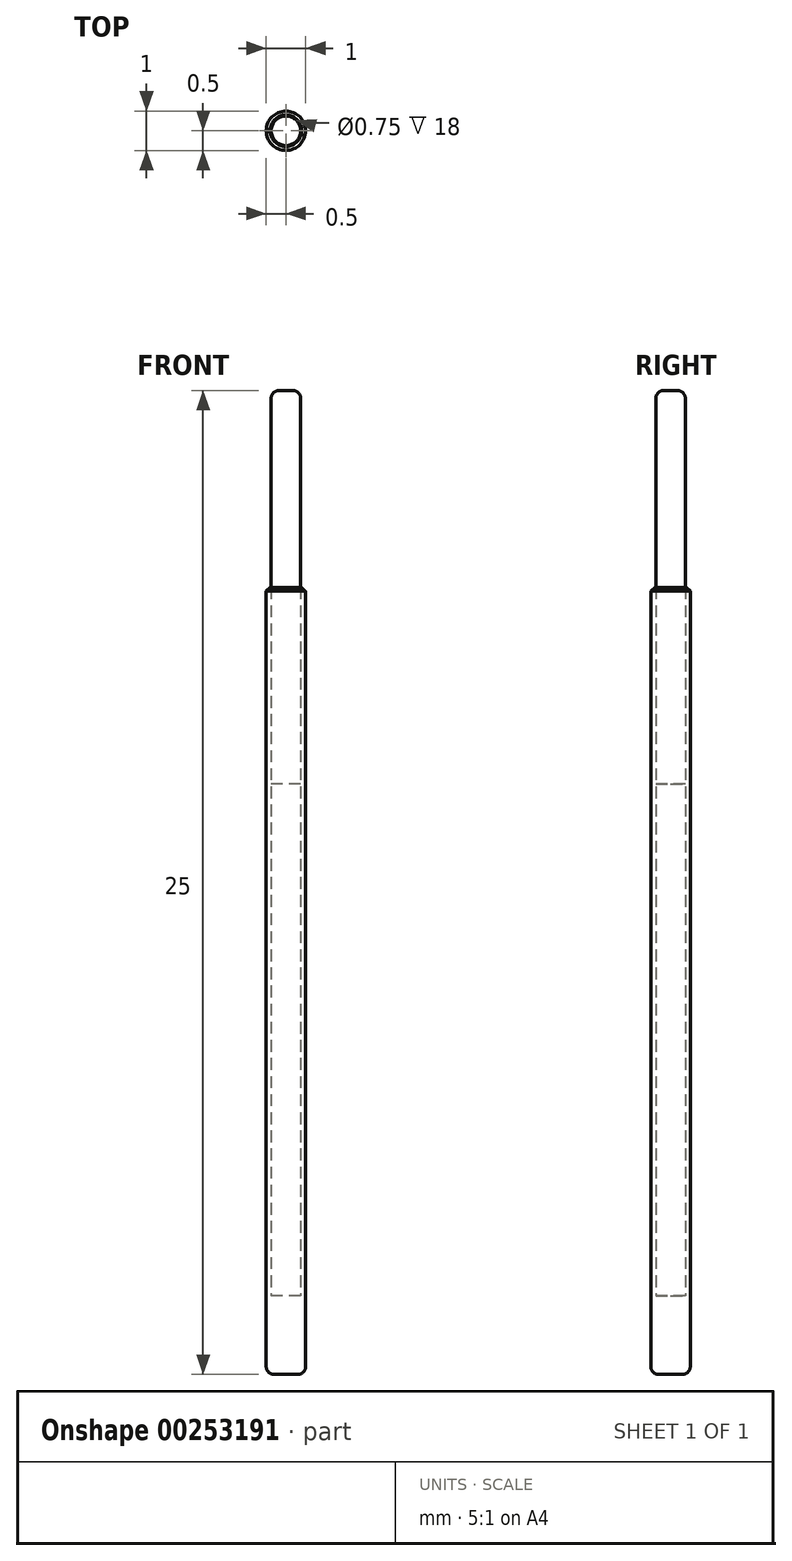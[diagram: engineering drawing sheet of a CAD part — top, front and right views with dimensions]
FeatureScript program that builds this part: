
annotation { "Feature Type Name" : "Feature", "Feature Type Description" : "" }
export const myFeature = defineFeature(function(context is Context, id is Id, definition is map)
    precondition{}
    {
        {
            var Q0;
            Q0=qCreatedBy(makeId("Top.planeOp"),FACE);
            var sketch = newSketch(context, id + "F0", { "sketchPlane" : qUnion([Q0])});
            skCircle(sketch, "E0", {"center": v(0, 0) * mm, "radius": 0.5 * mm});
            skCircle(sketch, "E1", {"center": v(0, 0) * mm, "radius": 0.38 * mm});
            skSolve(sketch);
        }
        {
            var Q0;
            Q0=makeQuery(id+"F0.imprint","IMPRINT",FACE,{"disambiguationData":[TD([[makeQuery(id+"F0.imprint","IMPRINT",EDGE,{"derivedFrom":sQuery(id+"F0.wireOp",EDGE,"E0")}),1.0]])]});
            extrude(context, id + "F1", {"entities" : qUnion([Q0]), "depth" : 20 * mm});
        }
        {
            var Q0;
            Q0=makeQuery(id+"F1.opExtrude","CAP_FACE",FACE,{"disambiguationData":[OSD([sQuery(id+"F0.wireOp",EDGE,"E0"),sQuery(id+"F0.wireOp",EDGE,"E1")])],"isStart":false});
            var sketch = newSketch(context, id + "F2", { "sketchPlane" : qUnion([Q0])});
            skCircle(sketch, "E2.0", {"center": v(0, 0) * mm, "radius": 0.38 * mm});
            skSolve(sketch);
        }
        {
            var Q0;
            Q0=makeQuery(id+"F2.imprint","IMPRINT",FACE,{"disambiguationData":[TD([[makeQuery(id+"F2.imprint","IMPRINT",EDGE,{"derivedFrom":sQuery(id+"F2.wireOp",EDGE,"E2.0")}),1.0]])]});
            extrude(context, id + "F3", {"entities" : qUnion([Q0]), "endBound" : BoundingType.SYMMETRIC, "depth" : 10 * mm});
        }
        {
            var Q0;
            Q0=makeQuery(id+"F3.opExtrude","CAP_EDGE",EDGE,{"disambiguationData":[OSD([sQuery(id+"F2.wireOp",EDGE,"E2.0")])],"isStart":false});
            fillet(context, id + "F4", {"entities" : qUnion([Q0]), "radius" : .2 * mm, "tangentPropagation" : true, "allowEdgeOverflow" : false});
        }
        {
            var Q0;
            Q0=makeQuery(id+"F1.opExtrude","CAP_EDGE",EDGE,{"disambiguationData":[OSD([sQuery(id+"F0.wireOp",EDGE,"E0")])],"isStart":false});
            chamfer(context, id + "F5", {"entities" : qUnion([Q0]), "width" : .1 * mm, "tangentPropagation" : true});
        }
        {
            var Q0;
            Q0=makeQuery(id+"F0.imprint","IMPRINT",FACE,{"disambiguationData":[TD([[makeQuery(id+"F0.imprint","IMPRINT",EDGE,{"derivedFrom":sQuery(id+"F0.wireOp",EDGE,"E1")}),1.0]])]});
            extrude(context, id + "F6", {"entities" : qUnion([Q0]), "operationType" : NewBodyOperationType.ADD, "depth" : 2 * mm});
        }
        {
            var Q0;
            Q0=makeQuery(id+"F1.opExtrude","CAP_EDGE",EDGE,{"disambiguationData":[OSD([sQuery(id+"F0.wireOp",EDGE,"E0")])],"isStart":true});
            fillet(context, id + "F7", {"entities" : qUnion([Q0]), "radius" : .2 * mm, "tangentPropagation" : true, "allowEdgeOverflow" : false});
        }
    });
